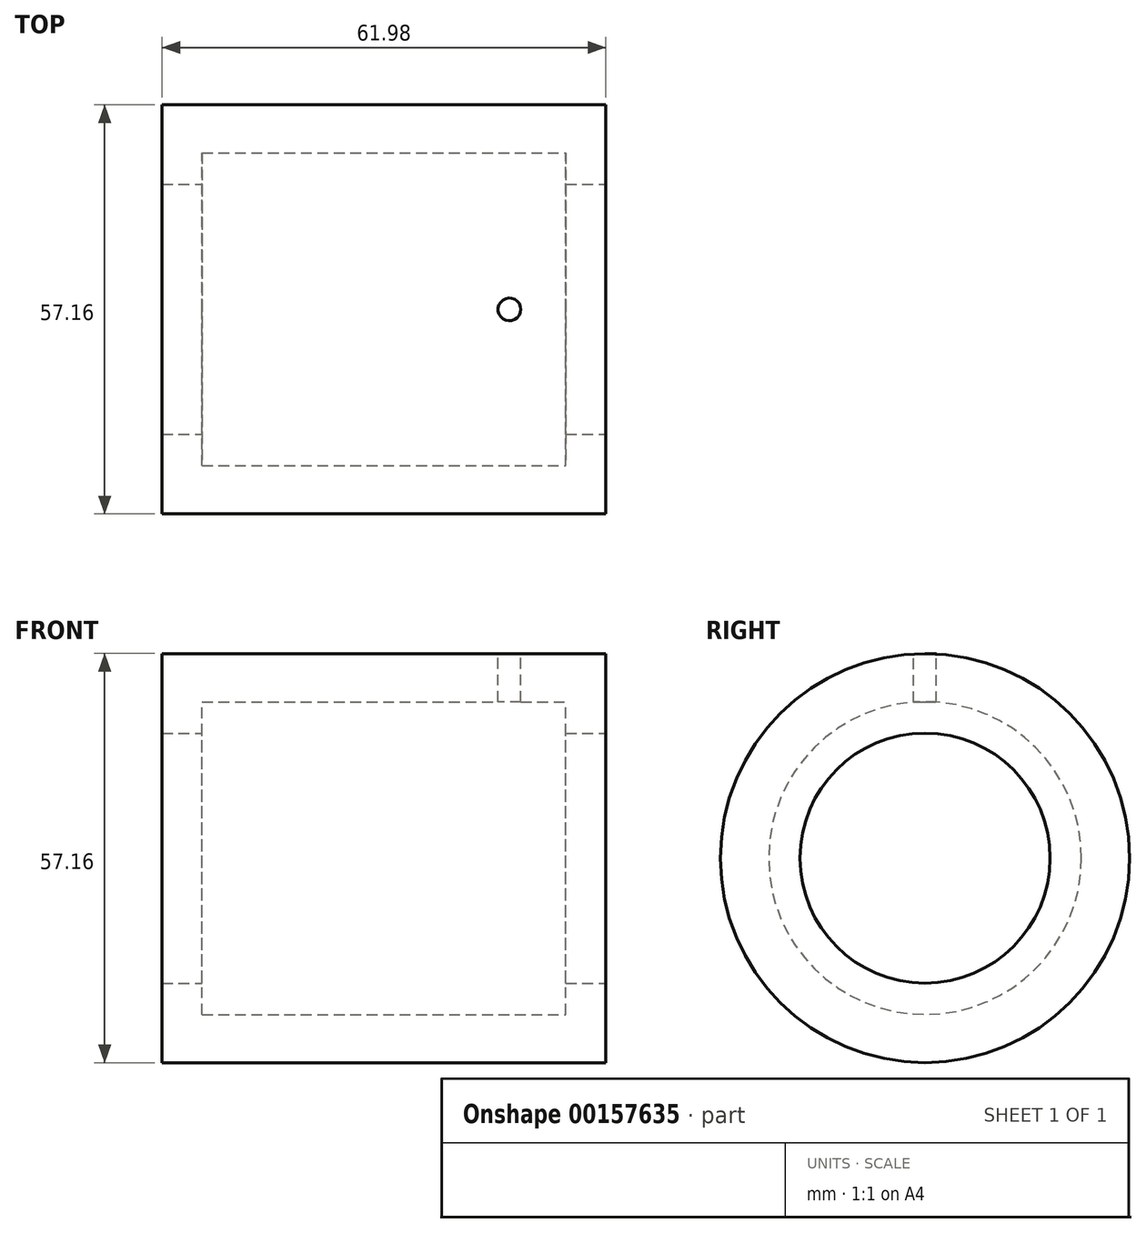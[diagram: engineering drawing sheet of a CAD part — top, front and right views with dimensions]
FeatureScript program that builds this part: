
annotation { "Feature Type Name" : "Feature", "Feature Type Description" : "" }
export const myFeature = defineFeature(function(context is Context, id is Id, definition is map)
    precondition{}
    {
        {
            var Q0;
            Q0=qCreatedBy(makeId("Right.planeOp"),FACE);
            var sketch = newSketch(context, id + "F0", { "sketchPlane" : qUnion([Q0])});
            skCircle(sketch, "E0", {"center": v(0, 0) * mm, "radius": 28.58 * mm});
            skCircle(sketch, "E1", {"center": v(0, 0) * mm, "radius": 17.46 * mm});
            skSolve(sketch);
        }
        {
            var Q0;
            Q0=makeQuery(id+"F0.imprint","IMPRINT",FACE,{"disambiguationData":[TD([[makeQuery(id+"F0.imprint","IMPRINT",EDGE,{"derivedFrom":sQuery(id+"F0.wireOp",EDGE,"E0")}),1.0]])]});
            extrude(context, id + "F1", {"entities" : qUnion([Q0]), "oppositeDirection" : true, "depth" : 61.98 * mm});
        }
        {
            var Q0;
            Q0=qCreatedBy(makeId("Right.planeOp"),FACE);
            cPlane(context, id + "F2", {"entities" : qUnion([Q0]), "cplaneType" : CPlaneType.OFFSET, "offset" : 5.6 * mm, "oppositeDirection" : true, "width" : 152.4 * mm, "height" : 152.4 * mm});
        }
        {
            var Q0;
            Q0=qCreatedBy(id+"F2.planeOp",FACE);
            var sketch = newSketch(context, id + "F3", { "sketchPlane" : qUnion([Q0])});
            skCircle(sketch, "E2", {"center": v(0, 0) * mm, "radius": 21.84 * mm});
            skSolve(sketch);
        }
        {
            var Q0;
            Q0=makeQuery(id+"F3.imprint","IMPRINT",FACE,{"disambiguationData":[TD([[makeQuery(id+"F3.imprint","IMPRINT",EDGE,{"derivedFrom":sQuery(id+"F3.wireOp",EDGE,"E2")}),1.0]])]});
            extrude(context, id + "F4", {"entities" : qUnion([Q0]), "operationType" : NewBodyOperationType.REMOVE, "oppositeDirection" : true, "depth" : 50.8 * mm});
        }
        {
            var Q0;
            Q0=makeQuery(id+"F1.opExtrude","CAP_FACE",FACE,{"disambiguationData":[OSD([sQuery(id+"F0.wireOp",EDGE,"E0"),sQuery(id+"F0.wireOp",EDGE,"E1")])],"isStart":true});
            var sketch = newSketch(context, id + "F5", { "sketchPlane" : qUnion([Q0])});
            skLineSegment(sketch, "E3", {"start": v(0, 17.46) * mm, "end": v(0, 28.58) * mm});
            skSolve(sketch);
        }
        {
            var Q0;
            Q0=sQuery(id+"F5.wireOp",EDGE,"E3");
            var Q1;
            Q1=sQuery(id+"F5.wireOp",VERTEX,"E3.end");
            cPlane(context, id + "F6", {"entities" : qUnion([Q0, Q1]), "cplaneType" : CPlaneType.LINE_POINT, "offset" : 25.4 * mm, "width" : 152.4 * mm, "height" : 152.4 * mm});
        }
        {
            var Q0;
            Q0=qCreatedBy(id+"F6.planeOp",FACE);
            var sketch = newSketch(context, id + "F7", { "sketchPlane" : qUnion([Q0])});
            skCircle(sketch, "E4", {"center": v(-13.46, 0) * mm, "radius": 1.59 * mm});
            skSolve(sketch);
        }
        {
            var Q0;
            Q0=makeQuery(id+"F7.imprint","IMPRINT",FACE,{"disambiguationData":[TD([[makeQuery(id+"F7.imprint","IMPRINT",EDGE,{"derivedFrom":sQuery(id+"F7.wireOp",EDGE,"E4")}),1.0]])]});
            extrude(context, id + "F8", {"entities" : qUnion([Q0]), "operationType" : NewBodyOperationType.REMOVE, "oppositeDirection" : true, "depth" : 12.7 * mm});
        }
    });
